FCSTD DOCUMENT  (FreeCAD 1.0R39319 (Git))
Label: portal-stepper-assembly
License: All rights reserved
LicenseURL: http://en.wikipedia.org/wiki/All_rights_reserved
objects: App::Link×4, App::FeaturePython×1, Assembly::JointGroup×1, Assembly::AssemblyObject×1
EXTERNAL_REF file=../../cnc-mill/NEMA23-holder.FCStd obj=Part
EXTERNAL_REF file=stepper-assembly.FCStd obj=Power_Step___PSM57HS2A54_2P
EXTERNAL_REF file=stepper-assembly.FCStd obj=ThreadedRod
EXTERNAL_REF file=stepper-assembly.FCStd obj=Coupler_6_35_8mm_Without_Screw

FEATURE [App::Link] nema23_holder  label="nema23-holder"
  LinkedObject = -> <external ../../cnc-mill/NEMA23-holder.FCStd>#Part
FEATURE [App::FeaturePython] GroundedJoint  # Assembly grounded joint (typed FeaturePython)
  ObjectToGround = -> nema23_holder
FEATURE [Assembly::JointGroup] Joints
  Group = -> [GroundedJoint]
FEATURE [App::Link] Power_Step___PSM57HS2A54_2P002  label="Power Step - PSM57HS2A54-2P002"
  LinkedObject = -> <external stepper-assembly.FCStd>#Power_Step___PSM57HS2A54_2P
FEATURE [App::Link] M8x400_ThreadedRod  label="M8x400-ThreadedRod"
  LinkPlacement = pos=(1.19563,-198.804,-198.804) rot=(1,0,0;1.5708rad)
  LinkedObject = -> <external stepper-assembly.FCStd>#ThreadedRod
  Placement = pos=(1.19563,-198.804,-198.804) rot=(1,0,0;1.5708rad)
FEATURE [App::Link] Coupler_6_35_8mm_Without_Screw001  label="Coupler 6.35-8mm Without Screw001"
  LinkPlacement = pos=(0,113.001,-0.000788718) rot=(1,0,0;1.5708rad)
  LinkedObject = -> <external stepper-assembly.FCStd>#Coupler_6_35_8mm_Without_Screw
  Placement = pos=(0,113.001,-0.000788718) rot=(1,0,0;1.5708rad)
FEATURE [Assembly::AssemblyObject] Assembly  label="portal-stepper-assembly"
  Group = -> [Joints,nema23_holder,GroundedJoint,Power_Step___PSM57HS2A54_2P002,M8x400_ThreadedRod,Coupler_6_35_8mm_Without_Screw001]
  Origin = -> Origin
  Type = Assembly
